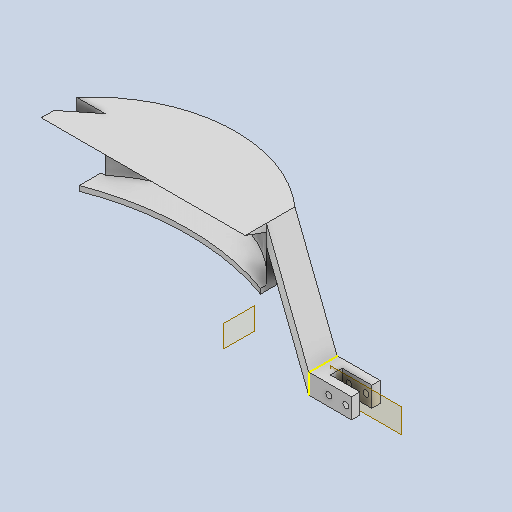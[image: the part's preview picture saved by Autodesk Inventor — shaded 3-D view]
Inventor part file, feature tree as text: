
AUTODESK INVENTOR PART (.ipt)
format: ipt  version: 2024.3 (Build 283343000, 343)  size: 158,720 bytes
history: native  units: mm
features: sketch x5, other x3, plane x2
ambient origin geometry x8: Origin, YZ Plane, XZ Plane, XY Plane, X Axis, Y Axis, Z Axis, Center Point
bodies: Solid1 (feature_tree)
feature tree (10):
  other  "pinzatula1.ipt"
  other  "Solid1::pinzatula1.ipt"
  other  "TaggingFeature1"
  sketch  "Sketch1"  dims[d0=10.0mm]
  sketch  "Sketch2"
  sketch  "Sketch3"
  sketch  "Sketch4"
  sketch  "Sketch5"
  plane  "Work Plane1"
  plane  "Work Plane2"
